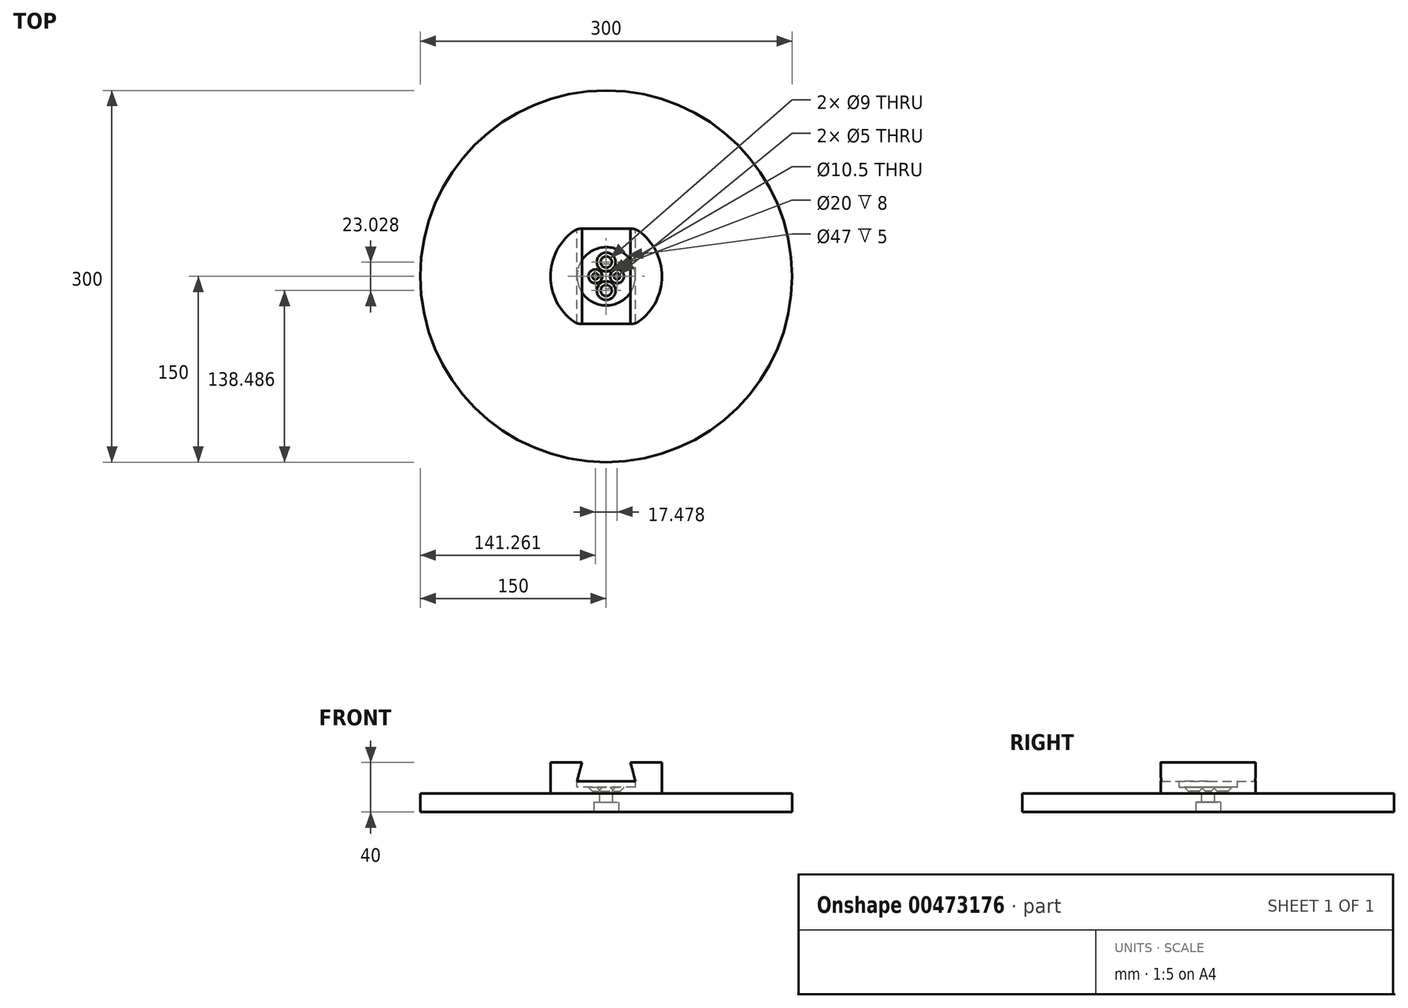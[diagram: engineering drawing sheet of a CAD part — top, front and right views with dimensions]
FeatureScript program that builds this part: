
annotation { "Feature Type Name" : "Feature", "Feature Type Description" : "" }
export const myFeature = defineFeature(function(context is Context, id is Id, definition is map)
    precondition{}
    {
        {
            assignVariable(context, id + "F0", {"name" : "Trou_Vis5mm", "anyValue" : 5});
        }
        {
            assignVariable(context, id + "F1", {"name" : "Trou_Vis9mm", "anyValue" : 9});
        }
        {
            assignVariable(context, id + "F2", {"name" : "Profondeur_Roulement", "anyValue" : 8});
        }
        {
            assignVariable(context, id + "F3", {"name" : "Epaisseur_Disque", "anyValue" : 15});
        }
        {
            var Q0;
            Q0=qCreatedBy(makeId("Top.planeOp"),FACE);
            var sketch = newSketch(context, id + "F4", { "sketchPlane" : qUnion([Q0])});
            skCircle(sketch, "E0", {"center": v(0, 0) * mm, "radius": 45 * mm});
            skLineSegment(sketch, "E1", {"start": v(-23.5, 38.38) * mm, "end": v(0, 38.38) * mm});
            skLineSegment(sketch, "E2", {"start": v(0, 38.38) * mm, "end": v(23.5, 38.38) * mm});
            skLineSegment(sketch, "E3.MirrorCS", {"start": v(-23.5, -38.38) * mm, "end": v(0, -38.38) * mm});
            skLineSegment(sketch, "E4.MirrorCS", {"start": v(0, -38.38) * mm, "end": v(23.5, -38.38) * mm});
            skLineSegment(sketch, "E5", {"start": v(-23.5, 38.38) * mm, "end": v(-23.5, -38.38) * mm});
            skLineSegment(sketch, "E6.MirrorCS", {"start": v(23.5, 38.38) * mm, "end": v(23.5, -38.38) * mm});
            skSolve(sketch);
        }
        {
            var Q0;
            {var subQ0=sQuery(id+"F4.wireOp",EDGE,"E5");Q0=makeQuery(id+"F4.imprint","IMPRINT",FACE,{"disambiguationData":[TD([[makeQuery(id+"F4.imprint","IMPRINT",EDGE,{"derivedFrom":subQ0}),-1.0]])]});}
            var Q1;
            {var subQ0=sQuery(id+"F4.wireOp",EDGE,"E6.MirrorCS");Q1=makeQuery(id+"F4.imprint","IMPRINT",FACE,{"disambiguationData":[TD([[makeQuery(id+"F4.imprint","IMPRINT",EDGE,{"derivedFrom":subQ0}),1.0]])]});}
            var Q2;
            Q2=makeQuery(id+"F4.imprint","IMPRINT",FACE,{"disambiguationData":[TD([[makeQuery(id+"F4.imprint","IMPRINT",EDGE,{"derivedFrom":sQuery(id+"F4.wireOp",EDGE,"E1")}),-1.0]])]});
            extrude(context, id + "F5", {"entities" : qUnion([Q0, Q1, Q2]), "depth" : 25 * mm, "offsetDistance" : 25 * mm});
        }
        {
            var Q0;
            Q0=makeQuery(id+"F5.opExtrude","SWEPT_FACE",FACE,{"disambiguationData":[OSD([sQuery(id+"F4.wireOp",EDGE,"E1"),sQuery(id+"F4.wireOp",EDGE,"E2")])]});
            var sketch = newSketch(context, id + "F6", { "sketchPlane" : qUnion([Q0])});
            skLineSegment(sketch, "E7", {"start": v(0, 0) * mm, "end": v(0, 10) * mm, "construction": true});
            skLineSegment(sketch, "E8", {"start": v(0, 10) * mm, "end": v(23.5, 10) * mm});
            skLineSegment(sketch, "E9", {"start": v(23.5, 10) * mm, "end": v(19.63, 25) * mm});
            skLineSegment(sketch, "E10.MirrorCS", {"start": v(0, 10) * mm, "end": v(-23.5, 10) * mm});
            skLineSegment(sketch, "E11.MirrorCS", {"start": v(-23.5, 10) * mm, "end": v(-19.63, 25) * mm});
            skLineSegment(sketch, "E12", {"start": v(19.63, 25) * mm, "end": v(-19.63, 25) * mm, "construction": true});
            skSolve(sketch);
        }
        {
            var Q0;
            Q0 = qSketchRegion(id + "F6", true);
            var Q1;
            Q1=makeQuery(id+"F6.imprint","IMPRINT",FACE,{"disambiguationData":[TD([[makeQuery(id+"F6.imprint","IMPRINT",EDGE,{"derivedFrom":sQuery(id+"F6.wireOp",EDGE,"E8")}),1.0]])]});
            extrude(context, id + "F7", {"entities" : qUnion([Q0, Q1]), "operationType" : NewBodyOperationType.REMOVE, "endBound" : BoundingType.THROUGH_ALL, "oppositeDirection" : true, "depth" : 25 * mm, "offsetDistance" : 25 * mm});
        }
        {
            var Q0;
            {var subQ0=sQuery(id+"F4.wireOp",EDGE,"E4.MirrorCS");var subQ1=sQuery(id+"F4.wireOp",EDGE,"E3.MirrorCS");var subQ2=sQuery(id+"F4.wireOp",EDGE,"E1");var subQ3=sQuery(id+"F4.wireOp",EDGE,"E0");var subQ4=sQuery(id+"F4.wireOp",EDGE,"E5");Q0=makeQuery(id+"F7.boolean.opBoolean","SPLIT",EDGE,{"disambiguationData":[TD([makeQuery(id+"F5.opExtrude","CAP_FACE",FACE,{"disambiguationData":[OSD([subQ3,subQ2,sQuery(id+"F4.wireOp",EDGE,"E2"),subQ1,subQ0])],"isStart":false})])],"derivedFrom":makeQuery(id+"F5.opExtrude","SWEPT_EDGE",EDGE,{"disambiguationData":[OSD([subQ3,subQ1,subQ4])]})});}
            var Q1;
            {var subQ0=sQuery(id+"F4.wireOp",EDGE,"E4.MirrorCS");var subQ1=sQuery(id+"F4.wireOp",EDGE,"E3.MirrorCS");var subQ2=sQuery(id+"F4.wireOp",EDGE,"E1");var subQ3=sQuery(id+"F4.wireOp",EDGE,"E0");var subQ4=sQuery(id+"F4.wireOp",EDGE,"E5");Q1=makeQuery(id+"F7.boolean.opBoolean","SPLIT",EDGE,{"disambiguationData":[TD([makeQuery(id+"F5.opExtrude","CAP_FACE",FACE,{"disambiguationData":[OSD([subQ3,subQ2,sQuery(id+"F4.wireOp",EDGE,"E2"),subQ1,subQ0])],"isStart":true})])],"derivedFrom":makeQuery(id+"F5.opExtrude","SWEPT_EDGE",EDGE,{"disambiguationData":[OSD([subQ3,subQ1,subQ4])]})});}
            var Q2;
            {var subQ0=sQuery(id+"F4.wireOp",EDGE,"E6.MirrorCS");var subQ1=sQuery(id+"F4.wireOp",EDGE,"E2");var subQ2=sQuery(id+"F4.wireOp",EDGE,"E0");var subQ3=sQuery(id+"F4.wireOp",EDGE,"E4.MirrorCS");var subQ4=sQuery(id+"F4.wireOp",EDGE,"E3.MirrorCS");Q2=makeQuery(id+"F7.boolean.opBoolean","SPLIT",EDGE,{"disambiguationData":[TD([makeQuery(id+"F5.opExtrude","CAP_FACE",FACE,{"disambiguationData":[OSD([subQ2,sQuery(id+"F4.wireOp",EDGE,"E1"),subQ1,subQ4,subQ3])],"isStart":false})])],"derivedFrom":makeQuery(id+"F5.opExtrude","SWEPT_EDGE",EDGE,{"disambiguationData":[OSD([subQ2,subQ3,subQ0])]})});}
            var Q3;
            {var subQ0=sQuery(id+"F4.wireOp",EDGE,"E6.MirrorCS");var subQ1=sQuery(id+"F4.wireOp",EDGE,"E2");var subQ2=sQuery(id+"F4.wireOp",EDGE,"E0");var subQ3=sQuery(id+"F4.wireOp",EDGE,"E4.MirrorCS");var subQ4=sQuery(id+"F4.wireOp",EDGE,"E3.MirrorCS");Q3=makeQuery(id+"F7.boolean.opBoolean","SPLIT",EDGE,{"disambiguationData":[TD([makeQuery(id+"F5.opExtrude","CAP_FACE",FACE,{"disambiguationData":[OSD([subQ2,sQuery(id+"F4.wireOp",EDGE,"E1"),subQ1,subQ4,subQ3])],"isStart":true})])],"derivedFrom":makeQuery(id+"F5.opExtrude","SWEPT_EDGE",EDGE,{"disambiguationData":[OSD([subQ2,subQ3,subQ0])]})});}
            var Q4;
            {var subQ0=sQuery(id+"F4.wireOp",EDGE,"E2");var subQ1=sQuery(id+"F4.wireOp",EDGE,"E1");var subQ2=sQuery(id+"F4.wireOp",EDGE,"E3.MirrorCS");var subQ3=sQuery(id+"F4.wireOp",EDGE,"E0");var subQ4=sQuery(id+"F4.wireOp",EDGE,"E5");Q4=makeQuery(id+"F7.boolean.opBoolean","SPLIT",EDGE,{"disambiguationData":[TD([makeQuery(id+"F5.opExtrude","CAP_FACE",FACE,{"disambiguationData":[OSD([subQ3,subQ1,subQ0,subQ2,sQuery(id+"F4.wireOp",EDGE,"E4.MirrorCS")])],"isStart":false})])],"derivedFrom":makeQuery(id+"F5.opExtrude","SWEPT_EDGE",EDGE,{"disambiguationData":[OSD([subQ3,subQ1,subQ4])]})});}
            var Q5;
            {var subQ0=sQuery(id+"F4.wireOp",EDGE,"E6.MirrorCS");var subQ1=sQuery(id+"F4.wireOp",EDGE,"E2");var subQ2=sQuery(id+"F4.wireOp",EDGE,"E0");var subQ3=sQuery(id+"F4.wireOp",EDGE,"E4.MirrorCS");var subQ4=sQuery(id+"F4.wireOp",EDGE,"E1");Q5=makeQuery(id+"F7.boolean.opBoolean","SPLIT",EDGE,{"disambiguationData":[TD([makeQuery(id+"F5.opExtrude","CAP_FACE",FACE,{"disambiguationData":[OSD([subQ2,subQ4,subQ1,sQuery(id+"F4.wireOp",EDGE,"E3.MirrorCS"),subQ3])],"isStart":false})])],"derivedFrom":makeQuery(id+"F5.opExtrude","SWEPT_EDGE",EDGE,{"disambiguationData":[OSD([subQ2,subQ1,subQ0])]})});}
            var Q6;
            {var subQ0=sQuery(id+"F4.wireOp",EDGE,"E6.MirrorCS");var subQ1=sQuery(id+"F4.wireOp",EDGE,"E2");var subQ2=sQuery(id+"F4.wireOp",EDGE,"E0");var subQ3=sQuery(id+"F4.wireOp",EDGE,"E4.MirrorCS");var subQ4=sQuery(id+"F4.wireOp",EDGE,"E1");Q6=makeQuery(id+"F7.boolean.opBoolean","SPLIT",EDGE,{"disambiguationData":[TD([makeQuery(id+"F5.opExtrude","CAP_FACE",FACE,{"disambiguationData":[OSD([subQ2,subQ4,subQ1,sQuery(id+"F4.wireOp",EDGE,"E3.MirrorCS"),subQ3])],"isStart":true})])],"derivedFrom":makeQuery(id+"F5.opExtrude","SWEPT_EDGE",EDGE,{"disambiguationData":[OSD([subQ2,subQ1,subQ0])]})});}
            var Q7;
            {var subQ0=sQuery(id+"F4.wireOp",EDGE,"E2");var subQ1=sQuery(id+"F4.wireOp",EDGE,"E1");var subQ2=sQuery(id+"F4.wireOp",EDGE,"E3.MirrorCS");var subQ3=sQuery(id+"F4.wireOp",EDGE,"E0");var subQ4=sQuery(id+"F4.wireOp",EDGE,"E5");Q7=makeQuery(id+"F7.boolean.opBoolean","SPLIT",EDGE,{"disambiguationData":[TD([makeQuery(id+"F5.opExtrude","CAP_FACE",FACE,{"disambiguationData":[OSD([subQ3,subQ1,subQ0,subQ2,sQuery(id+"F4.wireOp",EDGE,"E4.MirrorCS")])],"isStart":true})])],"derivedFrom":makeQuery(id+"F5.opExtrude","SWEPT_EDGE",EDGE,{"disambiguationData":[OSD([subQ3,subQ1,subQ4])]})});}
            fillet(context, id + "F8", {"entities" : qUnion([Q0, Q1, Q2, Q3, Q4, Q5, Q6, Q7]), "radius" : 10 * mm, "tangentPropagation" : true, "allowEdgeOverflow" : false});
        }
        {
            var Q0;
            Q0=makeQuery(id+"F7.boolean.opBoolean","COPY",FACE,{"derivedFrom":makeQuery(id+"F7.opExtrude","SWEPT_FACE",FACE,{"disambiguationData":[OSD([sQuery(id+"F6.wireOp",EDGE,"E8"),sQuery(id+"F6.wireOp",EDGE,"E10.MirrorCS")])]})});
            var sketch = newSketch(context, id + "F9", { "sketchPlane" : qUnion([Q0])});
            skCircle(sketch, "E13", {"center": v(0, 0) * mm, "radius": 23.5 * mm});
            skSolve(sketch);
        }
        {
            var Q0;
            Q0 = qSketchRegion(id + "F9", true);
            extrude(context, id + "F10", {"entities" : qUnion([Q0]), "operationType" : NewBodyOperationType.REMOVE, "oppositeDirection" : true, "depth" : 5 * mm, "offsetDistance" : 25 * mm});
        }
        {
            var Q0;
            Q0=makeQuery(id+"F10.boolean.opBoolean","COPY",FACE,{"derivedFrom":makeQuery(id+"F10.opExtrude","CAP_FACE",FACE,{"disambiguationData":[OSD([sQuery(id+"F9.wireOp",EDGE,"E13")])],"isStart":false})});
            var sketch = newSketch(context, id + "F11", { "sketchPlane" : qUnion([Q0])});
            skPoint(sketch, "E14", {"position": v(-8.74, 0) * mm});
            skPoint(sketch, "E15", {"position": v(0, 11.51) * mm});
            skPoint(sketch, "E16.MirrorP", {"position": v(8.74, 0) * mm});
            skPoint(sketch, "E17.MirrorP", {"position": v(0, -11.51) * mm});
            skSolve(sketch);
        }
        {
            var Q0;
            Q0=sQuery(id+"F11.wireOp",VERTEX,"E15");
            var Q1;
            Q1=sQuery(id+"F11.wireOp",VERTEX,"E17.MirrorP");
            var Q2;
            Q2=makeQuery(id+"F5.opExtrude","SWEPT_BODY",BODY,{"disambiguationData":[OSD([sQuery(id+"F4.wireOp",EDGE,"E0"),sQuery(id+"F4.wireOp",EDGE,"E1"),sQuery(id+"F4.wireOp",EDGE,"E2"),sQuery(id+"F4.wireOp",EDGE,"E3.MirrorCS"),sQuery(id+"F4.wireOp",EDGE,"E4.MirrorCS")])]});
            hole(context, id + "F12", {"style" : HoleStyle.C_SINK, "endStyle" : HoleEndStyle.THROUGH, "holeDiameter" : getVariable(context, 'Trou_Vis9mm') * mm, "cSinkDiameter" : 15.2 * mm, "cSinkAngle" : 90 * degree, "majorDiameter" : 5 * mm, "isTappedThrough" : true, "tappedDepth" : 12 * mm, "tapClearance" : 3, "locations" : qUnion([Q0, Q1]), "scope" : qUnion([Q2])});
        }
        {
            var Q0;
            Q0=sQuery(id+"F11.wireOp",VERTEX,"E14");
            var Q1;
            Q1=sQuery(id+"F11.wireOp",VERTEX,"E16.MirrorP");
            var Q2;
            Q2=makeQuery(id+"F5.opExtrude","SWEPT_BODY",BODY,{"disambiguationData":[OSD([sQuery(id+"F4.wireOp",EDGE,"E0"),sQuery(id+"F4.wireOp",EDGE,"E1"),sQuery(id+"F4.wireOp",EDGE,"E2"),sQuery(id+"F4.wireOp",EDGE,"E3.MirrorCS"),sQuery(id+"F4.wireOp",EDGE,"E4.MirrorCS")])]});
            hole(context, id + "F13", {"style" : HoleStyle.C_SINK, "endStyle" : HoleEndStyle.THROUGH, "holeDiameter" : (getVariable(context, 'Trou_Vis5mm')) * mm, "cSinkDiameter" : 11.2 * mm, "cSinkAngle" : 90 * degree, "majorDiameter" : 5 * mm, "isTappedThrough" : true, "tappedDepth" : 12 * mm, "tapClearance" : 3, "locations" : qUnion([Q0, Q1]), "scope" : qUnion([Q2])});
        }
        {
            var Q0;
            Q0=makeQuery(id+"F5.opExtrude","CAP_FACE",FACE,{"disambiguationData":[OSD([sQuery(id+"F4.wireOp",EDGE,"E0"),sQuery(id+"F4.wireOp",EDGE,"E1"),sQuery(id+"F4.wireOp",EDGE,"E2"),sQuery(id+"F4.wireOp",EDGE,"E3.MirrorCS"),sQuery(id+"F4.wireOp",EDGE,"E4.MirrorCS")])],"isStart":true});
            var sketch = newSketch(context, id + "F14", { "sketchPlane" : qUnion([Q0])});
            skCircle(sketch, "E18", {"center": v(0, 0) * mm, "radius": 150 * mm});
            skCircle(sketch, "E19", {"center": v(0, 0) * mm, "radius": 5.25 * mm});
            skSolve(sketch);
        }
        {
            var Q0;
            Q0 = qSketchRegion(id + "F14", true);
            var Q1;
            Q1=makeQuery(id+"F14.imprint","IMPRINT",FACE,{"disambiguationData":[TD([[makeQuery(id+"F14.imprint","IMPRINT",EDGE,{"derivedFrom":sQuery(id+"F14.wireOp",EDGE,"E19")}),-1.0]])]});
            var Q2;
            {var subQ0=sQuery(id+"F14.wireOp",EDGE,"5eb4fdb5-bccb-49eb-92cc-0b9e7f0527ec");var subQ1=makeQuery(id+"F13.hole-1.boolean.opBoolean","INTERSECT",EDGE,{"derivedFrom":[makeQuery(id+"F5.opExtrude","CAP_FACE",FACE,{"disambiguationData":[OSD([sQuery(id+"F4.wireOp",EDGE,"E0"),sQuery(id+"F4.wireOp",EDGE,"E1"),sQuery(id+"F4.wireOp",EDGE,"E2"),sQuery(id+"F4.wireOp",EDGE,"E3.MirrorCS"),sQuery(id+"F4.wireOp",EDGE,"E4.MirrorCS")])],"isStart":true}),makeQuery(id+"F13.hole-1.opRevolve","SWEPT_FACE",FACE,{"disambiguationData":[OSD([sQuery(id+"F13.hole-1.sketch.wireOp",EDGE,"core_line_2")])]})]});var subQ2=makeQuery(id+"F14.imprint","INTERSECT",VERTEX,{"disambiguationData":[OD(0.0)],"derivedFrom":[subQ1,subQ0]});Q2=makeQuery(id+"F14.imprint","IMPRINT",FACE,{"disambiguationData":[TD([[makeQuery(id+"F14.imprint","IMPRINT",EDGE,{"disambiguationData":[TD([[subQ2,1.0]])],"derivedFrom":subQ0}),1.0]])]});}
            var Q3;
            {var subQ0=sQuery(id+"F14.wireOp",EDGE,"5eb4fdb5-bccb-49eb-92cc-0b9e7f0527ec");var subQ1=makeQuery(id+"F12.hole-1.boolean.opBoolean","INTERSECT",EDGE,{"derivedFrom":[makeQuery(id+"F5.opExtrude","CAP_FACE",FACE,{"disambiguationData":[OSD([sQuery(id+"F4.wireOp",EDGE,"E0"),sQuery(id+"F4.wireOp",EDGE,"E1"),sQuery(id+"F4.wireOp",EDGE,"E2"),sQuery(id+"F4.wireOp",EDGE,"E3.MirrorCS"),sQuery(id+"F4.wireOp",EDGE,"E4.MirrorCS")])],"isStart":true}),makeQuery(id+"F12.hole-1.opRevolve","SWEPT_FACE",FACE,{"disambiguationData":[OSD([sQuery(id+"F12.hole-1.sketch.wireOp",EDGE,"core_line_2")])]})]});var subQ2=makeQuery(id+"F14.imprint","INTERSECT",VERTEX,{"disambiguationData":[OD(0.0)],"derivedFrom":[subQ1,subQ0]});Q3=makeQuery(id+"F14.imprint","IMPRINT",FACE,{"disambiguationData":[TD([[makeQuery(id+"F14.imprint","IMPRINT",EDGE,{"disambiguationData":[TD([[subQ2,-1.0]])],"derivedFrom":subQ0}),1.0]])]});}
            var Q4;
            {var subQ0=sQuery(id+"F14.wireOp",EDGE,"5eb4fdb5-bccb-49eb-92cc-0b9e7f0527ec");var subQ1=makeQuery(id+"F13.hole-0.boolean.opBoolean","INTERSECT",EDGE,{"derivedFrom":[makeQuery(id+"F5.opExtrude","CAP_FACE",FACE,{"disambiguationData":[OSD([sQuery(id+"F4.wireOp",EDGE,"E0"),sQuery(id+"F4.wireOp",EDGE,"E1"),sQuery(id+"F4.wireOp",EDGE,"E2"),sQuery(id+"F4.wireOp",EDGE,"E3.MirrorCS"),sQuery(id+"F4.wireOp",EDGE,"E4.MirrorCS")])],"isStart":true}),makeQuery(id+"F13.hole-0.opRevolve","SWEPT_FACE",FACE,{"disambiguationData":[OSD([sQuery(id+"F13.hole-0.sketch.wireOp",EDGE,"core_line_2")])]})]});var subQ2=makeQuery(id+"F14.imprint","INTERSECT",VERTEX,{"disambiguationData":[OD(0.0)],"derivedFrom":[subQ1,subQ0]});Q4=makeQuery(id+"F14.imprint","IMPRINT",FACE,{"disambiguationData":[TD([[makeQuery(id+"F14.imprint","IMPRINT",EDGE,{"disambiguationData":[TD([[subQ2,-1.0]])],"derivedFrom":subQ0}),1.0]])]});}
            var Q5;
            {var subQ0=sQuery(id+"F14.wireOp",EDGE,"5eb4fdb5-bccb-49eb-92cc-0b9e7f0527ec");var subQ1=makeQuery(id+"F12.hole-0.boolean.opBoolean","INTERSECT",EDGE,{"derivedFrom":[makeQuery(id+"F5.opExtrude","CAP_FACE",FACE,{"disambiguationData":[OSD([sQuery(id+"F4.wireOp",EDGE,"E0"),sQuery(id+"F4.wireOp",EDGE,"E1"),sQuery(id+"F4.wireOp",EDGE,"E2"),sQuery(id+"F4.wireOp",EDGE,"E3.MirrorCS"),sQuery(id+"F4.wireOp",EDGE,"E4.MirrorCS")])],"isStart":true}),makeQuery(id+"F12.hole-0.opRevolve","SWEPT_FACE",FACE,{"disambiguationData":[OSD([sQuery(id+"F12.hole-0.sketch.wireOp",EDGE,"core_line_2")])]})]});var subQ2=makeQuery(id+"F14.imprint","INTERSECT",VERTEX,{"disambiguationData":[OD(0.0)],"derivedFrom":[subQ1,subQ0]});Q5=makeQuery(id+"F14.imprint","IMPRINT",FACE,{"disambiguationData":[TD([[makeQuery(id+"F14.imprint","IMPRINT",EDGE,{"disambiguationData":[TD([[subQ2,-1.0]])],"derivedFrom":subQ0}),1.0]])]});}
            extrude(context, id + "F15", {"entities" : qUnion([Q0, Q1, Q2, Q3, Q4, Q5]), "depth" : (getVariable(context, 'Epaisseur_Disque')) * mm, "offsetDistance" : 25 * mm});
        }
        {
            var Q0;
            Q0=makeQuery(id+"F15.opExtrude","CAP_FACE",FACE,{"disambiguationData":[OSD([sQuery(id+"F14.wireOp",EDGE,"E18"),sQuery(id+"F14.wireOp",EDGE,"E19")])],"isStart":false});
            var sketch = newSketch(context, id + "F16", { "sketchPlane" : qUnion([Q0])});
            skCircle(sketch, "E20", {"center": v(0, 0) * mm, "radius": 10 * mm});
            skSolve(sketch);
        }
        {
            var Q0;
            Q0=makeQuery(id+"F16.imprint","IMPRINT",FACE,{"disambiguationData":[TD([[makeQuery(id+"F16.imprint","IMPRINT",EDGE,{"derivedFrom":sQuery(id+"F16.wireOp",EDGE,"E20")}),1.0]])]});
            extrude(context, id + "F17", {"entities" : qUnion([Q0]), "operationType" : NewBodyOperationType.REMOVE, "oppositeDirection" : true, "depth" : (getVariable(context, 'Profondeur_Roulement')) * mm, "offsetDistance" : 25 * mm});
        }
    });
